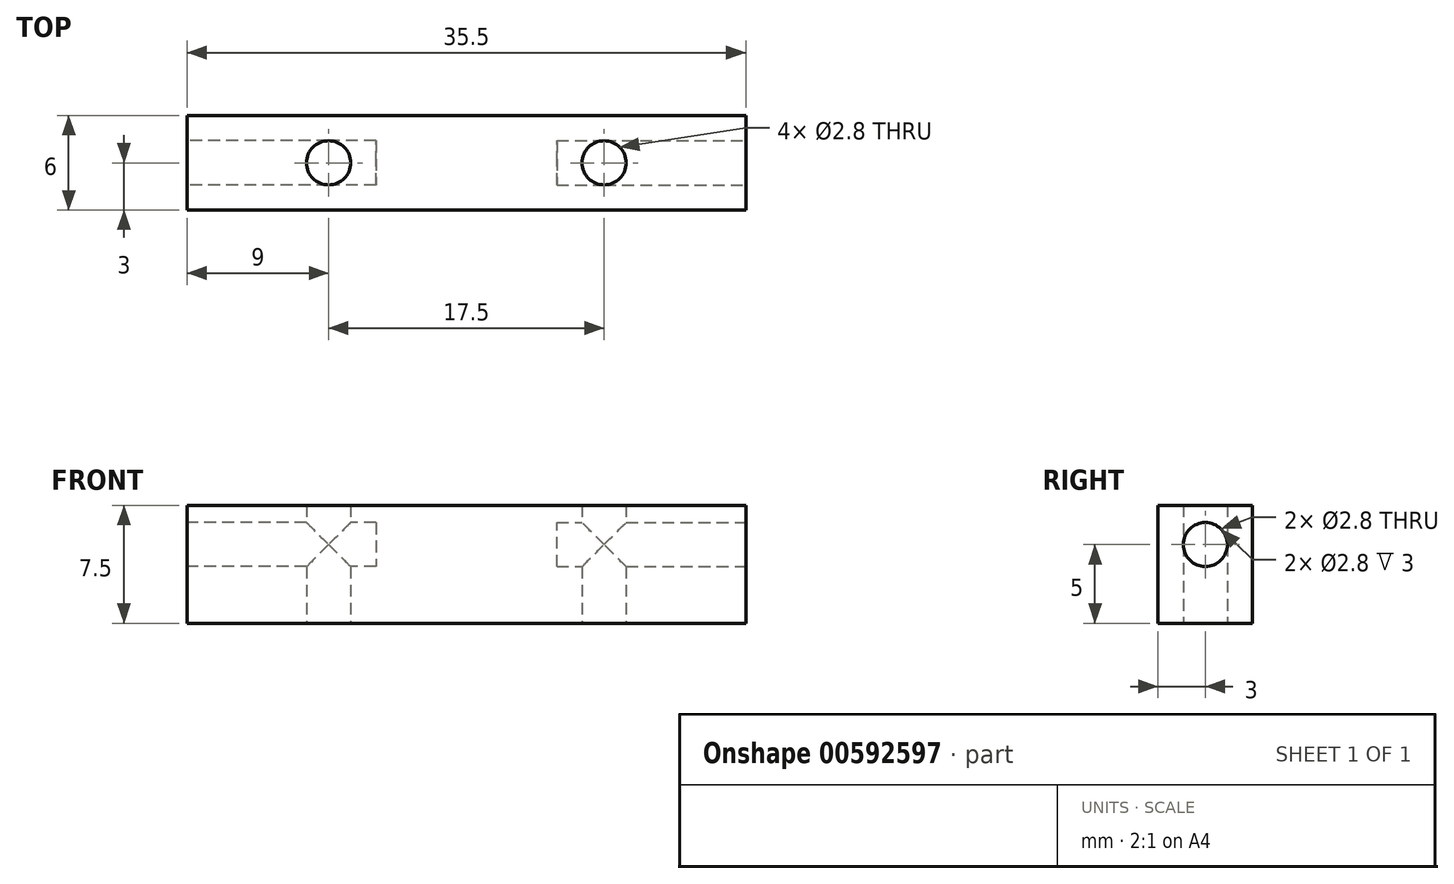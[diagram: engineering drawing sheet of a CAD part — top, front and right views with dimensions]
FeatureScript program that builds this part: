
annotation { "Feature Type Name" : "Feature", "Feature Type Description" : "" }
export const myFeature = defineFeature(function(context is Context, id is Id, definition is map)
    precondition{}
    {
        {
            var Q0;
            Q0=qCreatedBy(makeId("Top.planeOp"),FACE);
            var sketch = newSketch(context, id + "F0", { "sketchPlane" : qUnion([Q0])});
            skLineSegment(sketch, "E0.bottom", {"start": v(0, 0) * mm, "end": v(35.5, 0) * mm});
            skLineSegment(sketch, "E0.top", {"start": v(0, 6) * mm, "end": v(35.5, 6) * mm});
            skLineSegment(sketch, "E0.left", {"start": v(0, 0) * mm, "end": v(0, 6) * mm});
            skLineSegment(sketch, "E0.right", {"start": v(35.5, 0) * mm, "end": v(35.5, 6) * mm});
            skSolve(sketch);
        }
        {
            var Q0;
            Q0=makeQuery(id+"F0.imprint","IMPRINT",FACE,{"disambiguationData":[TD([[makeQuery(id+"F0.imprint","IMPRINT",EDGE,{"derivedFrom":sQuery(id+"F0.wireOp",EDGE,"E0.bottom")}),1.0]])]});
            extrude(context, id + "F1", {"entities" : qUnion([Q0]), "depth" : 7.5 * mm, "offsetDistance" : 25 * mm});
        }
        {
            var Q0;
            Q0=makeQuery(id+"F1.opExtrude","SWEPT_FACE",FACE,{"disambiguationData":[OSD([sQuery(id+"F0.wireOp",EDGE,"E0.right")])]});
            var sketch = newSketch(context, id + "F2", { "sketchPlane" : qUnion([Q0])});
            skLineSegment(sketch, "E1.0.0", {"start": v(0, 0) * mm, "end": v(6, 0) * mm});
            skLineSegment(sketch, "E1.0.1", {"start": v(6, 0) * mm, "end": v(6, 7.5) * mm});
            skLineSegment(sketch, "E1.0.2", {"start": v(6, 7.5) * mm, "end": v(0, 7.5) * mm});
            skLineSegment(sketch, "E1.0.3", {"start": v(0, 7.5) * mm, "end": v(0, 0) * mm});
            skCircle(sketch, "E2", {"center": v(3, 5) * mm, "radius": 1.4 * mm});
            skPoint(sketch, "E2.centerSnap0", {"position": v(3, 7.5) * mm});
            skSolve(sketch);
        }
        {
            var Q0;
            Q0=makeQuery(id+"F2.imprint","IMPRINT",FACE,{"disambiguationData":[TD([[makeQuery(id+"F2.imprint","IMPRINT",EDGE,{"derivedFrom":sQuery(id+"F2.wireOp",EDGE,"E2")}),1.0]])]});
            extrude(context, id + "F3", {"entities" : qUnion([Q0]), "operationType" : NewBodyOperationType.REMOVE, "oppositeDirection" : true, "depth" : 12 * mm, "offsetDistance" : 25 * mm});
        }
        {
            var Q0;
            Q0=makeQuery(id+"F1.opExtrude","SWEPT_FACE",FACE,{"disambiguationData":[OSD([sQuery(id+"F0.wireOp",EDGE,"E0.left")])]});
            var sketch = newSketch(context, id + "F4", { "sketchPlane" : qUnion([Q0])});
            skLineSegment(sketch, "E3.0.0", {"start": v(-6, 0) * mm, "end": v(0, 0) * mm});
            skLineSegment(sketch, "E3.0.1", {"start": v(0, 0) * mm, "end": v(0, 7.5) * mm});
            skLineSegment(sketch, "E3.0.2", {"start": v(0, 7.5) * mm, "end": v(-6, 7.5) * mm});
            skLineSegment(sketch, "E3.0.3", {"start": v(-6, 7.5) * mm, "end": v(-6, 0) * mm});
            skCircle(sketch, "E4", {"center": v(-3, 5) * mm, "radius": 1.4 * mm});
            skPoint(sketch, "E4.centerSnap0", {"position": v(-3, 7.5) * mm});
            skSolve(sketch);
        }
        {
            var Q0;
            Q0=makeQuery(id+"F4.imprint","IMPRINT",FACE,{"disambiguationData":[TD([[makeQuery(id+"F4.imprint","IMPRINT",EDGE,{"derivedFrom":sQuery(id+"F4.wireOp",EDGE,"E4")}),1.0]])]});
            extrude(context, id + "F5", {"entities" : qUnion([Q0]), "operationType" : NewBodyOperationType.REMOVE, "oppositeDirection" : true, "depth" : 12 * mm, "offsetDistance" : 25 * mm});
        }
        {
            var Q0;
            Q0=makeQuery(id+"F1.opExtrude","CAP_FACE",FACE,{"disambiguationData":[OSD([sQuery(id+"F0.wireOp",EDGE,"E0.bottom"),sQuery(id+"F0.wireOp",EDGE,"E0.top"),sQuery(id+"F0.wireOp",EDGE,"E0.left"),sQuery(id+"F0.wireOp",EDGE,"E0.right")])],"isStart":true});
            var sketch = newSketch(context, id + "F6", { "sketchPlane" : qUnion([Q0])});
            skLineSegment(sketch, "E5.0.0", {"start": v(0, -6) * mm, "end": v(35.5, -6) * mm});
            skLineSegment(sketch, "E5.0.1", {"start": v(35.5, -6) * mm, "end": v(35.5, 0) * mm});
            skLineSegment(sketch, "E5.0.2", {"start": v(35.5, 0) * mm, "end": v(0, 0) * mm});
            skLineSegment(sketch, "E5.0.3", {"start": v(0, 0) * mm, "end": v(0, -6) * mm});
            skCircle(sketch, "E6", {"center": v(9, -3) * mm, "radius": 1.4 * mm});
            skPoint(sketch, "E6.centerSnap0", {"position": v(0, -3) * mm});
            skCircle(sketch, "E7", {"center": v(26.5, -3) * mm, "radius": 1.4 * mm});
            skPoint(sketch, "E7.centerSnap0", {"position": v(35.5, -3) * mm});
            skSolve(sketch);
        }
        {
            var Q0;
            Q0=makeQuery(id+"F6.imprint","IMPRINT",FACE,{"disambiguationData":[TD([[makeQuery(id+"F6.imprint","IMPRINT",EDGE,{"derivedFrom":sQuery(id+"F6.wireOp",EDGE,"E6")}),1.0]])]});
            var Q1;
            Q1=makeQuery(id+"F6.imprint","IMPRINT",FACE,{"disambiguationData":[TD([[makeQuery(id+"F6.imprint","IMPRINT",EDGE,{"derivedFrom":sQuery(id+"F6.wireOp",EDGE,"E7")}),1.0]])]});
            var Q2;
            Q2=makeQuery(id+"F1.opExtrude","CAP_FACE",FACE,{"disambiguationData":[OSD([sQuery(id+"F0.wireOp",EDGE,"E0.bottom"),sQuery(id+"F0.wireOp",EDGE,"E0.top"),sQuery(id+"F0.wireOp",EDGE,"E0.left"),sQuery(id+"F0.wireOp",EDGE,"E0.right")])],"isStart":false});
            extrude(context, id + "F7", {"entities" : qUnion([Q0, Q1]), "operationType" : NewBodyOperationType.REMOVE, "endBound" : BoundingType.UP_TO_SURFACE, "oppositeDirection" : true, "depth" : 25 * mm, "endBoundEntityFace" : qUnion([Q2]), "offsetDistance" : 25 * mm});
        }
    });
